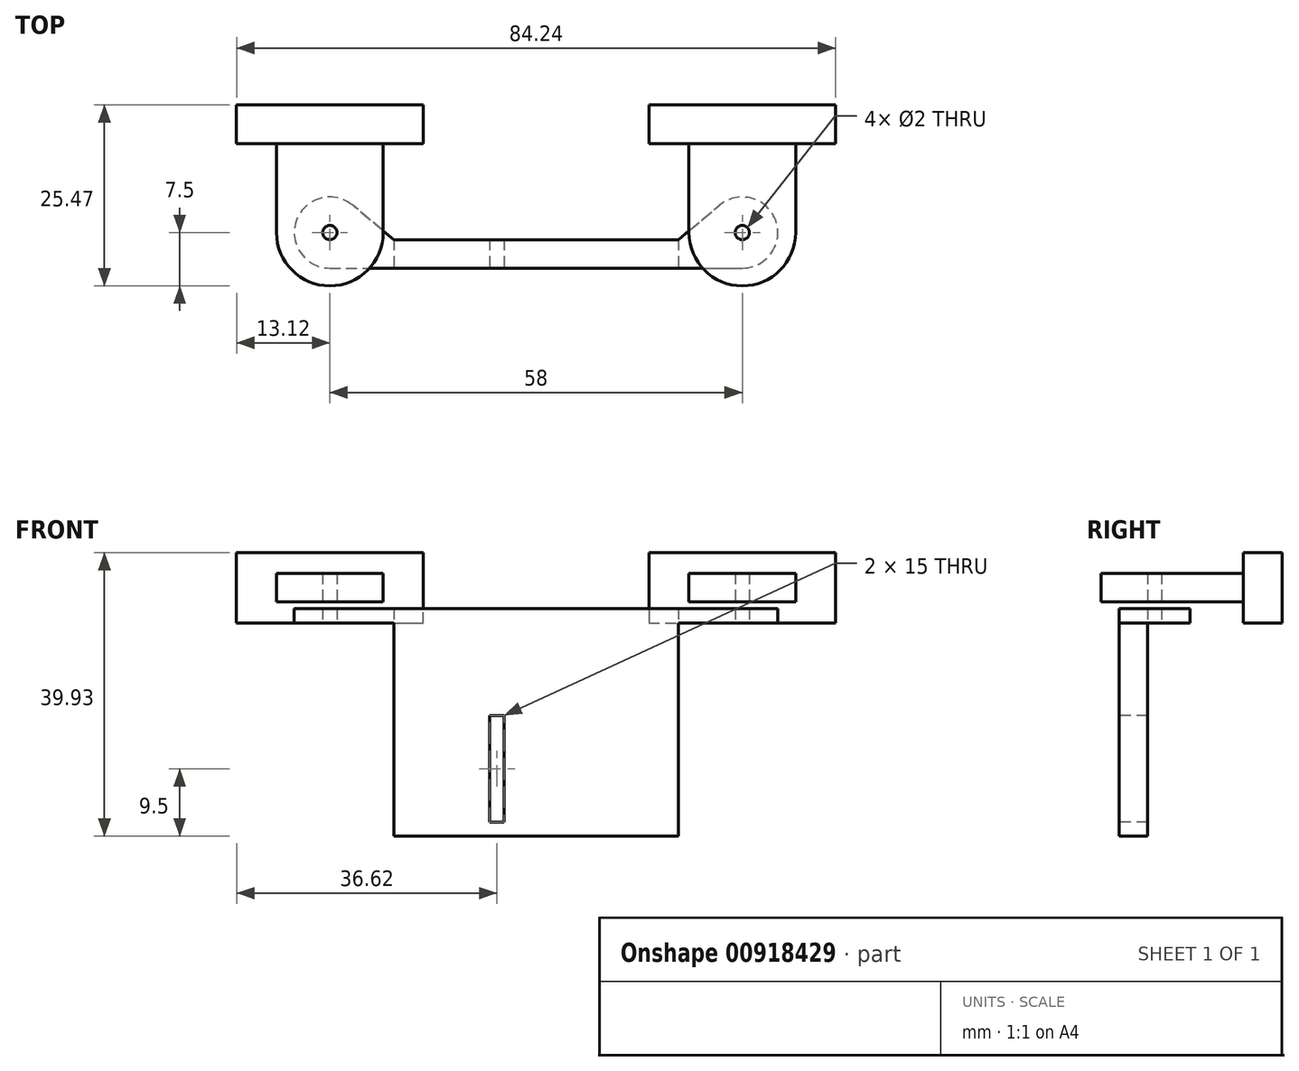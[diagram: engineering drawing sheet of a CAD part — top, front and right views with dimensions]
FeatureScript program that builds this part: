
annotation { "Feature Type Name" : "Feature", "Feature Type Description" : "" }
export const myFeature = defineFeature(function(context is Context, id is Id, definition is map)
    precondition{}
    {
        {
            assignVariable(context, id + "F0", {"name" : "LR_PlateHeight", "anyValue" : 30});
        }
        {
            var Q0;
            Q0=qCreatedBy(makeId("Front.planeOp"),FACE);
            var sketch = newSketch(context, id + "F1", { "sketchPlane" : qUnion([Q0])});
            skLineSegment(sketch, "E0.bottom", {"start": v(-42.12, 0) * mm, "end": v(-15.88, 0) * mm});
            skLineSegment(sketch, "E0.top", {"start": v(-42.12, 9.93) * mm, "end": v(-15.88, 9.93) * mm});
            skLineSegment(sketch, "E0.left", {"start": v(-42.12, 0) * mm, "end": v(-42.12, 9.93) * mm});
            skLineSegment(sketch, "E0.right", {"start": v(-15.88, 0) * mm, "end": v(-15.88, 9.93) * mm});
            skLineSegment(sketch, "E1.bottom", {"start": v(15.88, 9.93) * mm, "end": v(42.12, 9.93) * mm});
            skLineSegment(sketch, "E1.top", {"start": v(15.88, 0) * mm, "end": v(42.12, 0) * mm});
            skLineSegment(sketch, "E1.left", {"start": v(15.88, 9.93) * mm, "end": v(15.88, 0) * mm});
            skLineSegment(sketch, "E1.right", {"start": v(42.12, 9.93) * mm, "end": v(42.12, 0) * mm});
            skLineSegment(sketch, "E2", {"start": v(-29, 9.93) * mm, "end": v(-29, 0) * mm, "construction": true});
            skLineSegment(sketch, "E3", {"start": v(29, 9.93) * mm, "end": v(29, 0) * mm, "construction": true});
            skLineSegment(sketch, "E4.bottom", {"start": v(-36.5, 6.96) * mm, "end": v(-21.5, 6.96) * mm});
            skLineSegment(sketch, "E4.top", {"start": v(-36.5, 2.96) * mm, "end": v(-21.5, 2.96) * mm});
            skLineSegment(sketch, "E4.left", {"start": v(-36.5, 6.96) * mm, "end": v(-36.5, 2.96) * mm});
            skLineSegment(sketch, "E4.right", {"start": v(-21.5, 6.96) * mm, "end": v(-21.5, 2.96) * mm});
            skLineSegment(sketch, "E5.bottom", {"start": v(21.5, 6.96) * mm, "end": v(36.5, 6.96) * mm});
            skLineSegment(sketch, "E5.top", {"start": v(21.5, 2.96) * mm, "end": v(36.5, 2.96) * mm});
            skLineSegment(sketch, "E5.left", {"start": v(21.5, 6.96) * mm, "end": v(21.5, 2.96) * mm});
            skLineSegment(sketch, "E5.right", {"start": v(36.5, 6.96) * mm, "end": v(36.5, 2.96) * mm});
            skPoint(sketch, "E6", {"position": v(-29, 6.96) * mm});
            skPoint(sketch, "E7", {"position": v(29, 6.96) * mm});
            skPoint(sketch, "E8", {"position": v(-21.5, 4.96) * mm});
            skPoint(sketch, "E9", {"position": v(21.5, 4.96) * mm});
            skPoint(sketch, "E10", {"position": v(-15.88, 4.96) * mm});
            skPoint(sketch, "E11", {"position": v(15.88, 4.97) * mm});
            skLineSegment(sketch, "E12", {"start": v(-47.85, 4.96) * mm, "end": v(46.97, 4.96) * mm, "construction": true});
            skSolve(sketch);
        }
        {
            var Q0;
            Q0=makeQuery(id+"F1.imprint","IMPRINT",FACE,{"disambiguationData":[TD([[makeQuery(id+"F1.imprint","IMPRINT",EDGE,{"derivedFrom":sQuery(id+"F1.wireOp",EDGE,"E0.bottom")}),1.0]])]});
            var Q1;
            Q1=makeQuery(id+"F1.imprint","IMPRINT",FACE,{"disambiguationData":[TD([[makeQuery(id+"F1.imprint","IMPRINT",EDGE,{"derivedFrom":sQuery(id+"F1.wireOp",EDGE,"E1.bottom")}),-1.0]])]});
            extrude(context, id + "F2", {"entities" : qUnion([Q0, Q1]), "depth" : 5.47 * mm, "offsetDistance" : 25 * mm});
        }
        {
            var Q0;
            Q0=makeQuery(id+"F1.imprint","IMPRINT",FACE,{"disambiguationData":[TD([[makeQuery(id+"F1.imprint","IMPRINT",EDGE,{"derivedFrom":sQuery(id+"F1.wireOp",EDGE,"E4.bottom")}),-1.0]])]});
            var Q1;
            Q1=makeQuery(id+"F1.imprint","IMPRINT",FACE,{"disambiguationData":[TD([[makeQuery(id+"F1.imprint","IMPRINT",EDGE,{"derivedFrom":sQuery(id+"F1.wireOp",EDGE,"E5.bottom")}),-1.0]])]});
            extrude(context, id + "F3", {"entities" : qUnion([Q0, Q1]), "operationType" : NewBodyOperationType.ADD, "depth" : 25.47 * mm, "offsetDistance" : 25 * mm});
        }
        {
            var Q0;
            Q0=qCreatedBy(makeId("Top.planeOp"),FACE);
            var sketch = newSketch(context, id + "F4", { "sketchPlane" : qUnion([Q0])});
            skLineSegment(sketch, "E13.0", {"start": v(-36.5, -25.47) * mm, "end": v(-36.5, -5.47) * mm});
            skLineSegment(sketch, "E14.0", {"start": v(-21.5, -25.47) * mm, "end": v(-21.5, -5.47) * mm});
            skLineSegment(sketch, "E15.0", {"start": v(21.5, -25.47) * mm, "end": v(21.5, -5.47) * mm});
            skLineSegment(sketch, "E16.0", {"start": v(36.5, -25.47) * mm, "end": v(36.5, -5.47) * mm});
            skLineSegment(sketch, "E17.0", {"start": v(21.5, -25.47) * mm, "end": v(36.5, -25.47) * mm});
            skLineSegment(sketch, "E18.0", {"start": v(-36.5, -25.47) * mm, "end": v(-21.5, -25.47) * mm});
            skLineSegment(sketch, "E19", {"start": v(-36.5, -17.97) * mm, "end": v(36.5, -17.97) * mm, "construction": true});
            skLineSegment(sketch, "E20", {"start": v(-29, -25.47) * mm, "end": v(-29, 0) * mm, "construction": true});
            skLineSegment(sketch, "E21", {"start": v(29, -25.47) * mm, "end": v(29, 0) * mm, "construction": true});
            skCircle(sketch, "E22", {"center": v(-29, -17.97) * mm, "radius": 1 * mm});
            skCircle(sketch, "E23", {"center": v(29, -17.97) * mm, "radius": 1 * mm});
            skCircle(sketch, "E24", {"center": v(-29, -17.97) * mm, "radius": 5 * mm});
            skCircle(sketch, "E25", {"center": v(29, -17.97) * mm, "radius": 5 * mm});
            skArc(sketch, "E26", {"start": v(-36.5, -17.97) * mm, "mid": v(-29, -25.47) * mm, "end": v(-21.5, -17.97) * mm});
            skArc(sketch, "E27", {"start": v(21.5, -17.97) * mm, "mid": v(29, -25.47) * mm, "end": v(36.5, -17.97) * mm});
            skLineSegment(sketch, "E28", {"start": v(-29, -22.97) * mm, "end": v(29, -22.97) * mm});
            skLineSegment(sketch, "E29.bottom", {"start": v(-20, -18.97) * mm, "end": v(20, -18.97) * mm});
            skLineSegment(sketch, "E29.top", {"start": v(-20, -22.97) * mm, "end": v(20, -22.97) * mm});
            skLineSegment(sketch, "E29.left", {"start": v(-20, -18.97) * mm, "end": v(-20, -22.97) * mm});
            skLineSegment(sketch, "E29.right", {"start": v(20, -18.97) * mm, "end": v(20, -22.97) * mm});
            skPoint(sketch, "E30", {"position": v(0, -18.97) * mm});
            skLineSegment(sketch, "E31", {"start": v(-6.5, -18.97) * mm, "end": v(-6.5, -22.97) * mm});
            skLineSegment(sketch, "E32", {"start": v(-4.5, -18.97) * mm, "end": v(-4.5, -22.97) * mm});
            skLineSegment(sketch, "E33", {"start": v(-5.5, -12.97) * mm, "end": v(-5.5, -22.97) * mm, "construction": true});
            skLineSegment(sketch, "E34", {"start": v(-20, -18.97) * mm, "end": v(-25.8, -14.13) * mm});
            skLineSegment(sketch, "E35", {"start": v(20, -18.97) * mm, "end": v(25.8, -14.13) * mm});
            skSolve(sketch);
        }
        {
            var Q0;
            {var subQ0=sQuery(id+"F4.wireOp",EDGE,"E18.0");var subQ1=sQuery(id+"F4.wireOp",EDGE,"E13.0");var subQ2=makeQuery(id+"F4.imprint","INTERSECT",VERTEX,{"derivedFrom":[subQ1,subQ0]});Q0=makeQuery(id+"F4.imprint","IMPRINT",FACE,{"disambiguationData":[TD([[makeQuery(id+"F4.imprint","IMPRINT",EDGE,{"disambiguationData":[TD([[subQ2,-1.0]])],"derivedFrom":subQ1}),-1.0]])]});}
            var Q1;
            {var subQ0=sQuery(id+"F4.wireOp",EDGE,"E18.0");var subQ1=sQuery(id+"F4.wireOp",EDGE,"E14.0");var subQ2=makeQuery(id+"F4.imprint","INTERSECT",VERTEX,{"derivedFrom":[subQ1,subQ0]});Q1=makeQuery(id+"F4.imprint","IMPRINT",FACE,{"disambiguationData":[TD([[makeQuery(id+"F4.imprint","IMPRINT",EDGE,{"disambiguationData":[TD([[subQ2,-1.0]])],"derivedFrom":subQ1}),1.0]])]});}
            var Q2;
            {var subQ0=sQuery(id+"F4.wireOp",EDGE,"E17.0");var subQ1=sQuery(id+"F4.wireOp",EDGE,"E15.0");var subQ2=makeQuery(id+"F4.imprint","INTERSECT",VERTEX,{"derivedFrom":[subQ1,subQ0]});Q2=makeQuery(id+"F4.imprint","IMPRINT",FACE,{"disambiguationData":[TD([[makeQuery(id+"F4.imprint","IMPRINT",EDGE,{"disambiguationData":[TD([[subQ2,-1.0]])],"derivedFrom":subQ1}),-1.0]])]});}
            var Q3;
            {var subQ0=sQuery(id+"F4.wireOp",EDGE,"E17.0");var subQ1=sQuery(id+"F4.wireOp",EDGE,"E16.0");var subQ2=makeQuery(id+"F4.imprint","INTERSECT",VERTEX,{"derivedFrom":[subQ1,subQ0]});Q3=makeQuery(id+"F4.imprint","IMPRINT",FACE,{"disambiguationData":[TD([[makeQuery(id+"F4.imprint","IMPRINT",EDGE,{"disambiguationData":[TD([[subQ2,-1.0]])],"derivedFrom":subQ1}),1.0]])]});}
            var Q4;
            {var subQ0=sQuery(id+"F4.wireOp",EDGE,"E26");var subQ1=sQuery(id+"F4.wireOp",EDGE,"E14.0");var subQ2=makeQuery(id+"F4.imprint","INTERSECT",VERTEX,{"derivedFrom":[subQ1,subQ0]});Q4=makeQuery(id+"F4.imprint","IMPRINT",FACE,{"disambiguationData":[TD([[makeQuery(id+"F4.imprint","IMPRINT",EDGE,{"disambiguationData":[TD([[subQ2,1.0]])],"derivedFrom":subQ1}),1.0]])]});}
            var Q5;
            {var subQ0=sQuery(id+"F4.wireOp",EDGE,"E27");var subQ1=sQuery(id+"F4.wireOp",EDGE,"E15.0");var subQ2=makeQuery(id+"F4.imprint","INTERSECT",VERTEX,{"derivedFrom":[subQ1,subQ0]});Q5=makeQuery(id+"F4.imprint","IMPRINT",FACE,{"disambiguationData":[TD([[makeQuery(id+"F4.imprint","IMPRINT",EDGE,{"disambiguationData":[TD([[subQ2,1.0]])],"derivedFrom":subQ1}),-1.0]])]});}
            var Q6;
            Q6=makeQuery(id+"F4.imprint","IMPRINT",FACE,{"disambiguationData":[TD([[makeQuery(id+"F4.imprint","IMPRINT",EDGE,{"derivedFrom":sQuery(id+"F4.wireOp",EDGE,"E22")}),1.0]])]});
            var Q7;
            Q7=makeQuery(id+"F4.imprint","IMPRINT",FACE,{"disambiguationData":[TD([[makeQuery(id+"F4.imprint","IMPRINT",EDGE,{"derivedFrom":sQuery(id+"F4.wireOp",EDGE,"E23")}),1.0]])]});
            extrude(context, id + "F5", {"entities" : qUnion([Q0, Q1, Q2, Q3, Q4, Q5, Q6, Q7]), "operationType" : NewBodyOperationType.REMOVE, "depth" : 25 * mm, "offsetDistance" : 25 * mm});
        }
        {
            var Q0;
            {var subQ6=sQuery(id+"F4.wireOp",EDGE,"E14.0");var subQ7=makeQuery(id+"F4.imprint","INTERSECT",VERTEX,{"derivedFrom":[subQ6,sQuery(id+"F4.wireOp",EDGE,"E26")]});Q0=makeQuery(id+"F4.imprint","IMPRINT",FACE,{"disambiguationData":[TD([[makeQuery(id+"F4.imprint","IMPRINT",EDGE,{"disambiguationData":[TD([[subQ7,1.0]])],"derivedFrom":subQ6}),-1.0]])]});}
            var Q1;
            Q1=makeQuery(id+"F4.imprint","IMPRINT",FACE,{"disambiguationData":[TD([[makeQuery(id+"F4.imprint","IMPRINT",EDGE,{"derivedFrom":sQuery(id+"F4.wireOp",EDGE,"E22")}),-1.0]])]});
            var Q2;
            {var subQ3=sQuery(id+"F4.wireOp",EDGE,"E14.0");var subQ5=sQuery(id+"F4.wireOp",EDGE,"E26");var subQ6=makeQuery(id+"F4.imprint","INTERSECT",VERTEX,{"derivedFrom":[subQ3,subQ5]});Q2=makeQuery(id+"F4.imprint","IMPRINT",FACE,{"disambiguationData":[TD([[makeQuery(id+"F4.imprint","IMPRINT",EDGE,{"disambiguationData":[TD([[subQ6,-1.0]])],"derivedFrom":subQ3}),1.0]])]});}
            var Q3;
            Q3=makeQuery(id+"F4.imprint","IMPRINT",FACE,{"disambiguationData":[TD([[makeQuery(id+"F4.imprint","IMPRINT",EDGE,{"derivedFrom":sQuery(id+"F4.wireOp",EDGE,"E23")}),-1.0]])]});
            var Q4;
            {var subQ3=sQuery(id+"F4.wireOp",EDGE,"E15.0");var subQ5=sQuery(id+"F4.wireOp",EDGE,"E27");var subQ6=makeQuery(id+"F4.imprint","INTERSECT",VERTEX,{"derivedFrom":[subQ3,subQ5]});Q4=makeQuery(id+"F4.imprint","IMPRINT",FACE,{"disambiguationData":[TD([[makeQuery(id+"F4.imprint","IMPRINT",EDGE,{"disambiguationData":[TD([[subQ6,-1.0]])],"derivedFrom":subQ3}),-1.0]])]});}
            var Q5;
            {var subQ0=sQuery(id+"F4.wireOp",EDGE,"E27");var subQ1=sQuery(id+"F4.wireOp",EDGE,"E15.0");var subQ2=makeQuery(id+"F4.imprint","INTERSECT",VERTEX,{"derivedFrom":[subQ1,subQ0]});Q5=makeQuery(id+"F4.imprint","IMPRINT",FACE,{"disambiguationData":[TD([[makeQuery(id+"F4.imprint","IMPRINT",EDGE,{"disambiguationData":[TD([[subQ2,1.0]])],"derivedFrom":subQ1}),-1.0]])]});}
            var Q6;
            {var subQ0=sQuery(id+"F4.wireOp",EDGE,"E26");var subQ1=sQuery(id+"F4.wireOp",EDGE,"E14.0");var subQ2=makeQuery(id+"F4.imprint","INTERSECT",VERTEX,{"derivedFrom":[subQ1,subQ0]});Q6=makeQuery(id+"F4.imprint","IMPRINT",FACE,{"disambiguationData":[TD([[makeQuery(id+"F4.imprint","IMPRINT",EDGE,{"disambiguationData":[TD([[subQ2,1.0]])],"derivedFrom":subQ1}),1.0]])]});}
            var Q7;
            {var subQ0=sQuery(id+"F4.wireOp",EDGE,"E29.right");Q7=makeQuery(id+"F4.imprint","IMPRINT",FACE,{"disambiguationData":[TD([[makeQuery(id+"F4.imprint","IMPRINT",EDGE,{"derivedFrom":subQ0}),1.0]])]});}
            extrude(context, id + "F6", {"entities" : qUnion([Q0, Q1, Q2, Q3, Q4, Q5, Q6, Q7]), "depth" : 2 * mm, "offsetDistance" : 25 * mm});
        }
        {
            var Q0;
            {var subQ0=sQuery(id+"F4.wireOp",EDGE,"E29.left");Q0=makeQuery(id+"F4.imprint","IMPRINT",FACE,{"disambiguationData":[TD([[makeQuery(id+"F4.imprint","IMPRINT",EDGE,{"derivedFrom":subQ0}),1.0]])]});}
            var Q1;
            {var subQ0=sQuery(id+"F4.wireOp",EDGE,"E29.right");Q1=makeQuery(id+"F4.imprint","IMPRINT",FACE,{"disambiguationData":[TD([[makeQuery(id+"F4.imprint","IMPRINT",EDGE,{"derivedFrom":subQ0}),-1.0]])]});}
            extrude(context, id + "F7", {"entities" : qUnion([Q0, Q1]), "operationType" : NewBodyOperationType.ADD, "oppositeDirection" : true, "depth" : (getVariable(context, 'LR_PlateHeight')) * mm, "offsetDistance" : 25 * mm, "hasSecondDirection" : true, "secondDirectionOppositeDirection" : false, "secondDirectionDepth" : 2 * mm});
        }
        {
            var Q0;
            {var subQ0=sQuery(id+"F4.wireOp",EDGE,"E31");Q0=makeQuery(id+"F4.imprint","IMPRINT",FACE,{"disambiguationData":[TD([[makeQuery(id+"F4.imprint","IMPRINT",EDGE,{"derivedFrom":subQ0}),1.0]])]});}
            extrude(context, id + "F8", {"entities" : qUnion([Q0]), "operationType" : NewBodyOperationType.ADD, "depth" : 2 * mm, "offsetDistance" : 25 * mm, "hasSecondDirection" : true, "secondDirectionOppositeDirection" : true, "secondDirectionDepth" : (getVariable(context, 'LR_PlateHeight') - 17) * mm});
        }
        {
            var Q0;
            {var subQ0=sQuery(id+"F4.wireOp",EDGE,"E31");Q0=makeQuery(id+"F4.imprint","IMPRINT",FACE,{"disambiguationData":[TD([[makeQuery(id+"F4.imprint","IMPRINT",EDGE,{"derivedFrom":subQ0}),1.0]])]});}
            extrude(context, id + "F9", {"entities" : qUnion([Q0]), "operationType" : NewBodyOperationType.ADD, "oppositeDirection" : true, "depth" : (getVariable(context, 'LR_PlateHeight')) * mm, "offsetDistance" : 25 * mm, "hasSecondDirection" : true, "secondDirectionOppositeDirection" : true, "secondDirectionDepth" : (getVariable(context, 'LR_PlateHeight') - 2) * mm});
        }
    });
